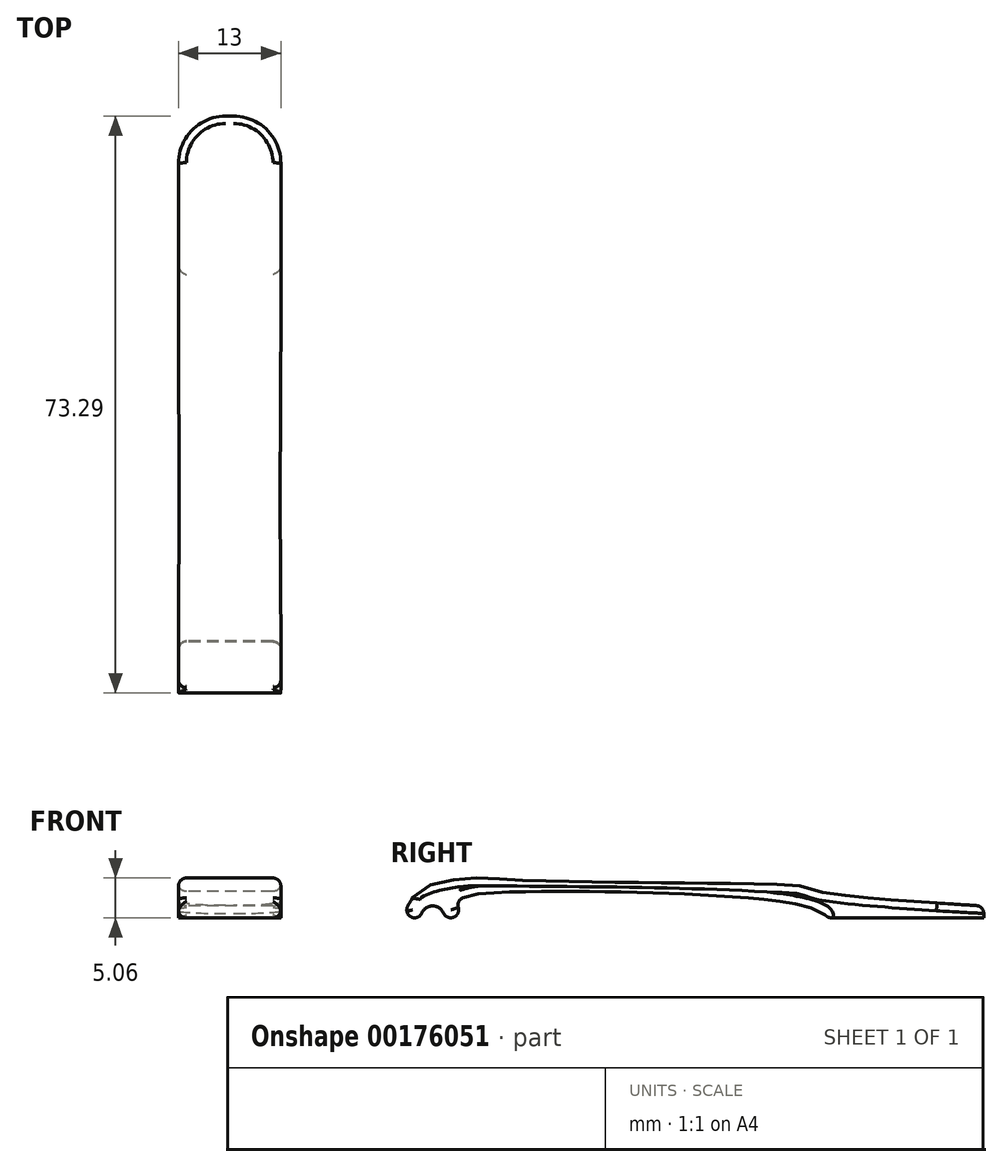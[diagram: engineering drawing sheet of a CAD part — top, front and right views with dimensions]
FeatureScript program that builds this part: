
annotation { "Feature Type Name" : "Feature", "Feature Type Description" : "" }
export const myFeature = defineFeature(function(context is Context, id is Id, definition is map)
    precondition{}
    {
        {
            var Q0;
            Q0=qCreatedBy(makeId("Right.planeOp"),FACE);
            var sketch = newSketch(context, id + "F0", { "sketchPlane" : qUnion([Q0])});
            skLineSegment(sketch, "E0", {"start": v(0, 0) * mm, "end": v(20, 0) * mm});
            skLineSegment(sketch, "E1", {"start": v(20, 0) * mm, "end": v(20, 1.5) * mm});
            skPoint(sketch, "E2", {"position": v(-50, 0) * mm});
            skLineSegment(sketch, "E3", {"start": v(0, 0) * mm, "end": v(-50, 0) * mm, "construction": true});
            skFitSpline(sketch, "E4", {"points": [v(-51.71, 0.82) * mm, v(-48.09, 4.7) * mm, v(-38.87, 4.77) * mm, v(-4.21, 4.14) * mm, v(20, 1.5) * mm], "startDerivative": vector(-55.88, 50.27) * mm, "endDerivative": vector(272.27, -16.2) * mm});
            skFitSpline(sketch, "E5", {"points": [v(0, 0) * mm, v(-38.87, 3.3) * mm, v(-45.46, 2.78) * mm, v(-48.36, 1.27) * mm], "startDerivative": vector(0, 16.08) * mm, "endDerivative": vector(-30.55, -19.41) * mm});
            skArc(sketch, "E6", {"start": v(-48.5, 0) * mm, "mid": v(-50, 1.5) * mm, "end": v(-51.5, 0) * mm});
            skArc(sketch, "E7.0", {"start": v(-46.5, 0) * mm, "mid": v(-46.66, 1.06) * mm, "end": v(-47.14, 2.02) * mm});
            skLineSegment(sketch, "E8", {"start": v(-48.5, 0) * mm, "end": v(-46.5, 0) * mm});
            skLineSegment(sketch, "E9", {"start": v(-51.5, 0) * mm, "end": v(-53.5, 0) * mm});
            skPoint(sketch, "E10.end.orphan", {"position": v(-48.36, 1.5) * mm});
            skArc(sketch, "E11.trimOffspring", {"start": v(-52.62, 2.32) * mm, "mid": v(-53.27, 1.24) * mm, "end": v(-53.5, 0) * mm});
            skSolve(sketch);
        }
        {
            var Q0;
            Q0 = qSketchRegion(id + "F0", true);
            extrude(context, id + "F1", {"entities" : qUnion([Q0]), "depth" : 13 * mm});
        }
        {
            var Q0;
            Q0=makeQuery(id+"F1.opExtrude","CAP_EDGE",EDGE,{"disambiguationData":[OSD([sQuery(id+"F0.wireOp",EDGE,"E1")])],"isStart":false});
            var Q1;
            Q1=makeQuery(id+"F1.opExtrude","CAP_EDGE",EDGE,{"disambiguationData":[OSD([sQuery(id+"F0.wireOp",EDGE,"E1")])],"isStart":true});
            fillet(context, id + "F2", {"entities" : qUnion([Q0, Q1]), "radius" : 6 * mm, "tangentPropagation" : true, "allowEdgeOverflow" : false});
        }
        {
            var Q0;
            Q0=makeQuery(id+"F1.opExtrude","SWEPT_FACE",FACE,{"disambiguationData":[OSD([sQuery(id+"F0.wireOp",EDGE,"E4")])]});
            var Q1;
            Q1=makeQuery(id+"F1.opExtrude","SWEPT_FACE",FACE,{"disambiguationData":[OSD([sQuery(id+"F0.wireOp",EDGE,"E5")])]});
            fillet(context, id + "F3", {"entities" : qUnion([Q0, Q1]), "radius" : 1 * mm, "tangentPropagation" : true, "allowEdgeOverflow" : false});
        }
        {
            var Q0;
            Q0=makeQuery(id+"F1.opExtrude","SWEPT_FACE",FACE,{"disambiguationData":[OSD([sQuery(id+"F0.wireOp",EDGE,"E9")])]});
            var Q1;
            Q1=makeQuery(id+"F1.opExtrude","SWEPT_FACE",FACE,{"disambiguationData":[OSD([sQuery(id+"F0.wireOp",EDGE,"E8")])]});
            var Q2;
            Q2=makeQuery(id+"F1.opExtrude","CAP_EDGE",EDGE,{"disambiguationData":[OSD([sQuery(id+"F0.wireOp",EDGE,"E6")])],"isStart":true});
            var Q3;
            Q3=makeQuery(id+"F1.opExtrude","CAP_EDGE",EDGE,{"disambiguationData":[OSD([sQuery(id+"F0.wireOp",EDGE,"E6")])],"isStart":false});
            fillet(context, id + "F4", {"entities" : qUnion([Q0, Q1, Q2, Q3]), "radius" : 1 * mm, "tangentPropagation" : true, "allowEdgeOverflow" : false});
        }
    });
